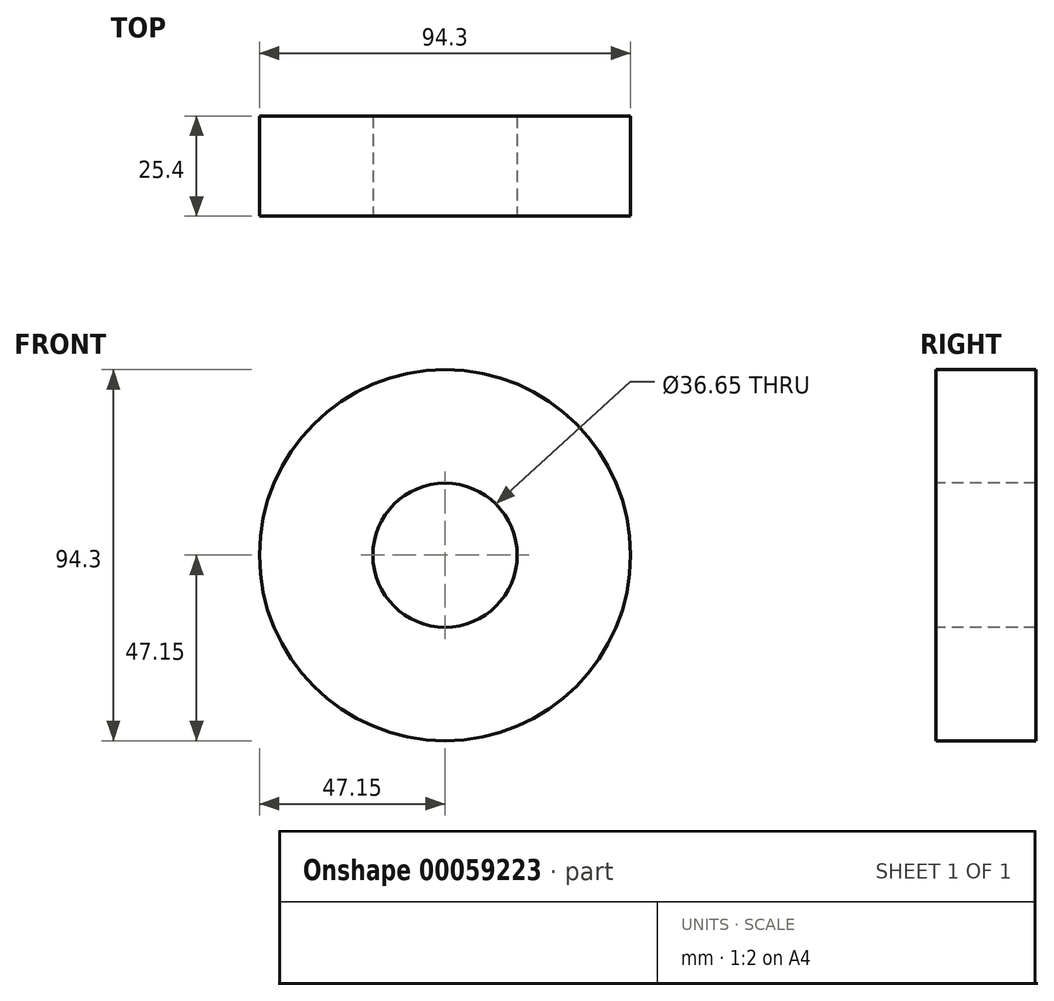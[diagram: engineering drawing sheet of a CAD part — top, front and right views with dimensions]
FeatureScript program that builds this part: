
annotation { "Feature Type Name" : "Feature", "Feature Type Description" : "" }
export const myFeature = defineFeature(function(context is Context, id is Id, definition is map)
    precondition{}
    {
        {
            var Q0;
            Q0=qCreatedBy(makeId("Front.planeOp"),FACE);
            var sketch = newSketch(context, id + "F0", { "sketchPlane" : qUnion([Q0])});
            skCircle(sketch, "E0", {"center": v(0, 0) * mm, "radius": 74.96 * mm});
            skSolve(sketch);
        }
        {
            var Q0;
            Q0=makeQuery(id+"F0.imprint","IMPRINT",FACE,{"disambiguationData":[TD([[makeQuery(id+"F0.imprint","IMPRINT",EDGE,{"derivedFrom":sQuery(id+"F0.wireOp",EDGE,"E0")}),1.0]])]});
            extrude(context, id + "F1", {"entities" : qUnion([Q0]), "depth" : 25.4 * mm});
        }
        {
            var Q0;
            Q0=makeQuery(id+"F1.opExtrude","CAP_FACE",FACE,{"disambiguationData":[OSD([sQuery(id+"F0.wireOp",EDGE,"E0")])],"isStart":false});
            var sketch = newSketch(context, id + "F2", { "sketchPlane" : qUnion([Q0])});
            skCircle(sketch, "E1", {"center": v(0, 0) * mm, "radius": 47.15 * mm});
            skSolve(sketch);
        }
        {
            var Q0;
            Q0=makeQuery(id+"F2.imprint","IMPRINT",FACE,{"disambiguationData":[TD([[makeQuery(id+"F2.imprint","IMPRINT",EDGE,{"derivedFrom":sQuery(id+"F2.wireOp",EDGE,"E1")}),1.0]])]});
            extrude(context, id + "F3", {"entities" : qUnion([Q0]), "operationType" : NewBodyOperationType.INTERSECT, "oppositeDirection" : true, "depth" : 25.4 * mm});
        }
        {
            var Q0;
            Q0=makeQuery(id+"F1.opExtrude","CAP_FACE",FACE,{"disambiguationData":[OSD([sQuery(id+"F0.wireOp",EDGE,"E0")])],"isStart":false});
            var sketch = newSketch(context, id + "F5", { "sketchPlane" : qUnion([Q0])});
            skCircle(sketch, "E2", {"center": v(0, 0) * mm, "radius": 18.32 * mm});
            skSolve(sketch);
        }
        {
            var Q0;
            Q0=makeQuery(id+"F5.imprint","IMPRINT",FACE,{"disambiguationData":[TD([[makeQuery(id+"F5.imprint","IMPRINT",EDGE,{"derivedFrom":sQuery(id+"F5.wireOp",EDGE,"E2")}),1.0]])]});
            extrude(context, id + "F4", {"entities" : qUnion([Q0]), "operationType" : NewBodyOperationType.REMOVE, "oppositeDirection" : true, "depth" : 73.66 * mm});
        }
    });
